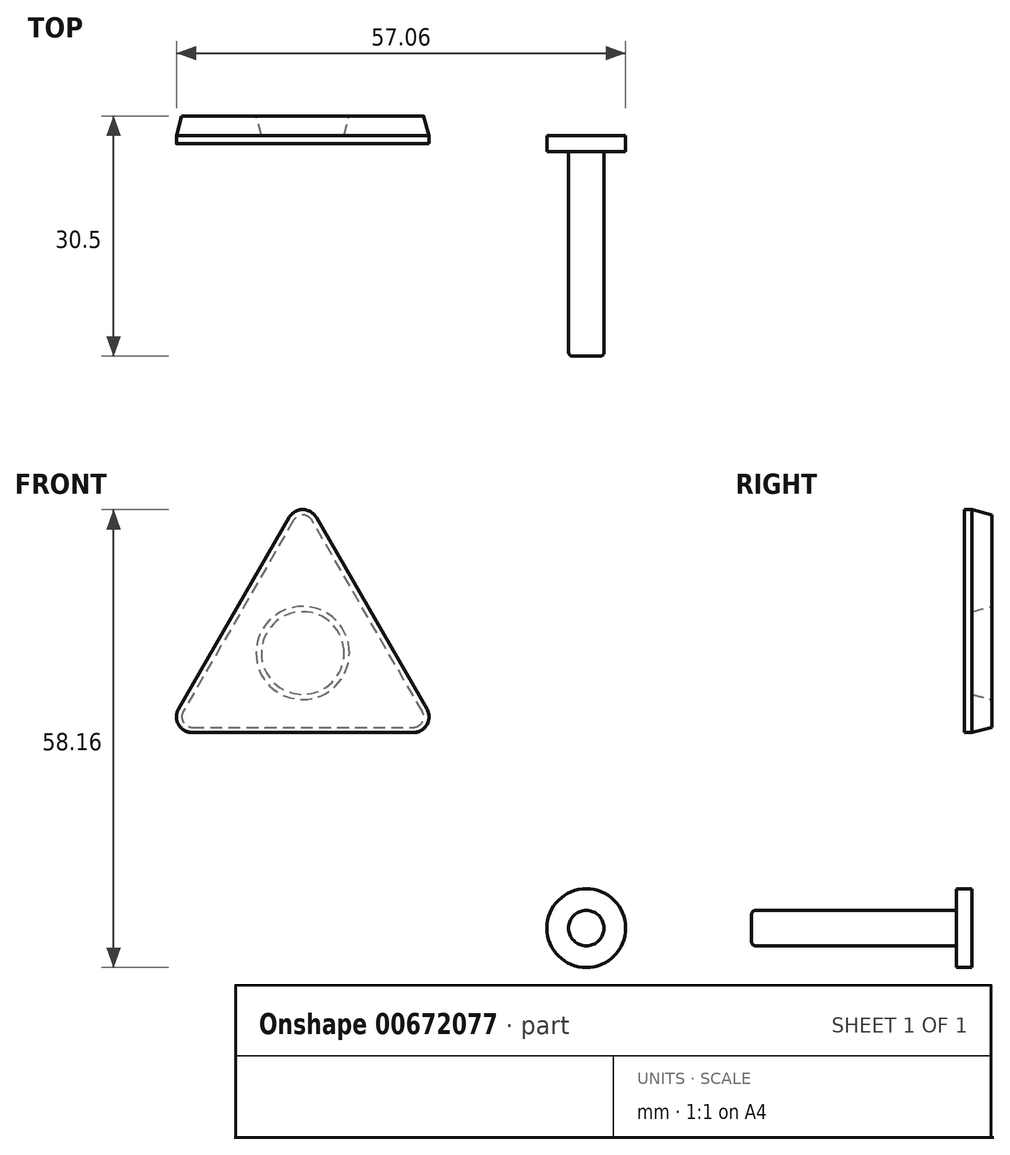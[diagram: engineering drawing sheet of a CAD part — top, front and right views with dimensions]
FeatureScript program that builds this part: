
annotation { "Feature Type Name" : "Feature", "Feature Type Description" : "" }
export const myFeature = defineFeature(function(context is Context, id is Id, definition is map)
    precondition{}
    {
        {
            var Q0;
            Q0=qCreatedBy(makeId("Front.planeOp"),FACE);
            var sketch = newSketch(context, id + "F0", { "sketchPlane" : qUnion([Q0])});
            skCircle(sketch, "E0", {"center": v(0, 0) * mm, "radius": 5 * mm});
            skCircle(sketch, "E1", {"center": v(0, 0) * mm, "radius": 2.25 * mm});
            skSolve(sketch);
        }
        {
            var Q0;
            Q0=makeQuery(id+"F0.imprint","IMPRINT",FACE,{"disambiguationData":[TD([[makeQuery(id+"F0.imprint","IMPRINT",EDGE,{"derivedFrom":sQuery(id+"F0.wireOp",EDGE,"E1")}),1.0]])]});
            extrude(context, id + "F1", {"entities" : qUnion([Q0]), "depth" : 28 * mm, "offsetDistance" : 25 * mm});
        }
        {
            var Q0;
            Q0=makeQuery(id+"F0.imprint","IMPRINT",FACE,{"disambiguationData":[TD([[makeQuery(id+"F0.imprint","IMPRINT",EDGE,{"derivedFrom":sQuery(id+"F0.wireOp",EDGE,"E0")}),1.0]])]});
            extrude(context, id + "F2", {"entities" : qUnion([Q0]), "operationType" : NewBodyOperationType.ADD, "depth" : 2 * mm, "offsetDistance" : 25 * mm});
        }
        {
            var Q0;
            Q0=makeQuery(id+"F1.opExtrude","CAP_EDGE",EDGE,{"disambiguationData":[OSD([sQuery(id+"F0.wireOp",EDGE,"E1")])],"isStart":false});
            fillet(context, id + "F3", {"entities" : qUnion([Q0]), "radius" : .5 * mm, "tangentPropagation" : true, "allowEdgeOverflow" : false});
        }
        {
            var Q0;
            Q0=qCreatedBy(makeId("Front.planeOp"),FACE);
            var sketch = newSketch(context, id + "F4", { "sketchPlane" : qUnion([Q0])});
            skLineSegment(sketch, "E2", {"start": v(-34.29, 52.15) * mm, "end": v(-20.25, 27.84) * mm});
            skLineSegment(sketch, "E3", {"start": v(-21.98, 24.84) * mm, "end": v(-50.05, 24.84) * mm});
            skLineSegment(sketch, "E4", {"start": v(-51.79, 27.84) * mm, "end": v(-37.75, 52.15) * mm});
            skPoint(sketch, "E5.visualSharp", {"position": v(-36.02, 55.15) * mm});
            skArc(sketch, "E5.filletArc", {"start": v(-34.29, 52.15) * mm, "mid": v(-36.02, 53.15) * mm, "end": v(-37.75, 52.15) * mm});
            skPoint(sketch, "E6.visualSharp", {"position": v(-18.52, 24.84) * mm});
            skArc(sketch, "E6.filletArc", {"start": v(-21.98, 24.84) * mm, "mid": v(-20.25, 25.84) * mm, "end": v(-20.25, 27.84) * mm});
            skPoint(sketch, "E7.visualSharp", {"position": v(-53.52, 24.84) * mm});
            skArc(sketch, "E7.filletArc", {"start": v(-51.79, 27.84) * mm, "mid": v(-51.79, 25.84) * mm, "end": v(-50.05, 24.84) * mm});
            skCircle(sketch, "E8", {"center": v(-36.02, 34.94) * mm, "radius": 5.25 * mm});
            skSolve(sketch);
        }
        {
            var Q0;
            Q0=makeQuery(id+"F4.imprint","IMPRINT",FACE,{"disambiguationData":[TD([[makeQuery(id+"F4.imprint","IMPRINT",EDGE,{"derivedFrom":sQuery(id+"F4.wireOp",EDGE,"E2")}),-1.0]])]});
            extrude(context, id + "F5", {"entities" : qUnion([Q0]), "oppositeDirection" : true, "depth" : 2.5 * mm, "offsetDistance" : 25 * mm, "hasDraft" : true, "draftAngle" : 15 * degree, "draftPullDirection" : true});
        }
        {
            var Q0;
            Q0=qCreatedBy(makeId("Front.planeOp"),FACE);
            var sketch = newSketch(context, id + "F6", { "sketchPlane" : qUnion([Q0])});
            skLineSegment(sketch, "E9", {"start": v(-37.76, 52.16) * mm, "end": v(-51.8, 27.85) * mm});
            skLineSegment(sketch, "E10", {"start": v(-50.06, 24.85) * mm, "end": v(-22, 24.85) * mm});
            skLineSegment(sketch, "E11", {"start": v(-20.26, 27.85) * mm, "end": v(-34.3, 52.16) * mm});
            skPoint(sketch, "E12.visualSharp", {"position": v(-36.03, 55.16) * mm});
            skArc(sketch, "E12.filletArc", {"start": v(-34.3, 52.16) * mm, "mid": v(-36.03, 53.16) * mm, "end": v(-37.76, 52.16) * mm});
            skPoint(sketch, "E13.visualSharp", {"position": v(-18.53, 24.85) * mm});
            skArc(sketch, "E13.filletArc", {"start": v(-22, 24.85) * mm, "mid": v(-20.26, 25.85) * mm, "end": v(-20.26, 27.85) * mm});
            skPoint(sketch, "E14.visualSharp", {"position": v(-53.53, 24.85) * mm});
            skArc(sketch, "E14.filletArc", {"start": v(-51.8, 27.85) * mm, "mid": v(-51.8, 25.85) * mm, "end": v(-50.06, 24.85) * mm});
            skSolve(sketch);
        }
        {
            var Q0;
            Q0=makeQuery(id+"F6.imprint","IMPRINT",FACE,{"disambiguationData":[TD([[makeQuery(id+"F6.imprint","IMPRINT",EDGE,{"derivedFrom":sQuery(id+"F6.wireOp",EDGE,"E9")}),1.0]])]});
            extrude(context, id + "F7", {"entities" : qUnion([Q0]), "operationType" : NewBodyOperationType.ADD, "depth" : 1 * mm, "offsetDistance" : 25 * mm});
        }
    });
